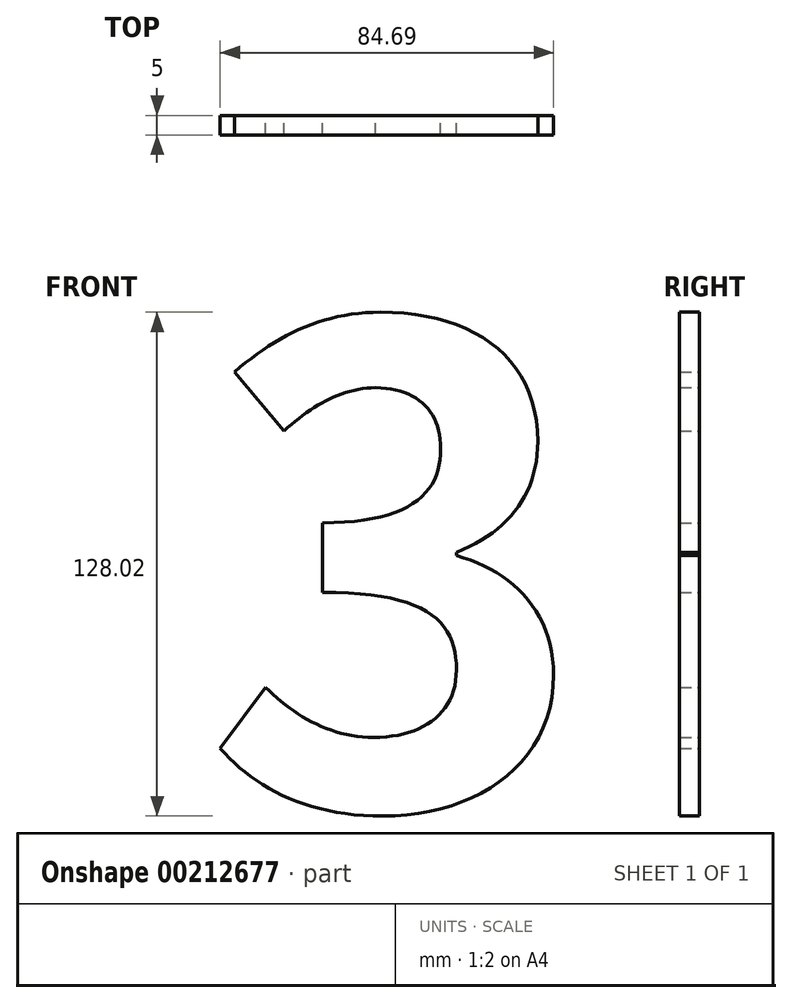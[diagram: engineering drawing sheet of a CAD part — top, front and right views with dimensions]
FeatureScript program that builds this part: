
annotation { "Feature Type Name" : "Feature", "Feature Type Description" : "" }
export const myFeature = defineFeature(function(context is Context, id is Id, definition is map)
    precondition{}
    {
        {
            var Q0;
            Q0=qCreatedBy(makeId("Front.planeOp"),FACE);
            var sketch = newSketch(context, id + "F0", { "sketchPlane" : qUnion([Q0])});
            skText(sketch, "E0", { "text": "3", "fontName": "NotoSansCJKsc-Bold.otf"});
            const initialGuessF0  = {"E0": [-0.06419, -0.06708, 1, 0, 0.12]};
            skSetInitialGuess(sketch, initialGuessF0);
            skSolve(sketch);
        }
        {
            var Q0;
            Q0=makeQuery(id+"F0.imprint","IMPRINT",FACE,{"disambiguationData":[TD([[makeQuery(id+"F0.imprint","IMPRINT",EDGE,{"derivedFrom":sQuery(id+"F0.wireOp",EDGE,"E0.sketch_text.stroke-0")}),1.0]])]});
            extrude(context, id + "F1", {"entities" : qUnion([Q0]), "depth" : 5 * mm});
        }
    });
